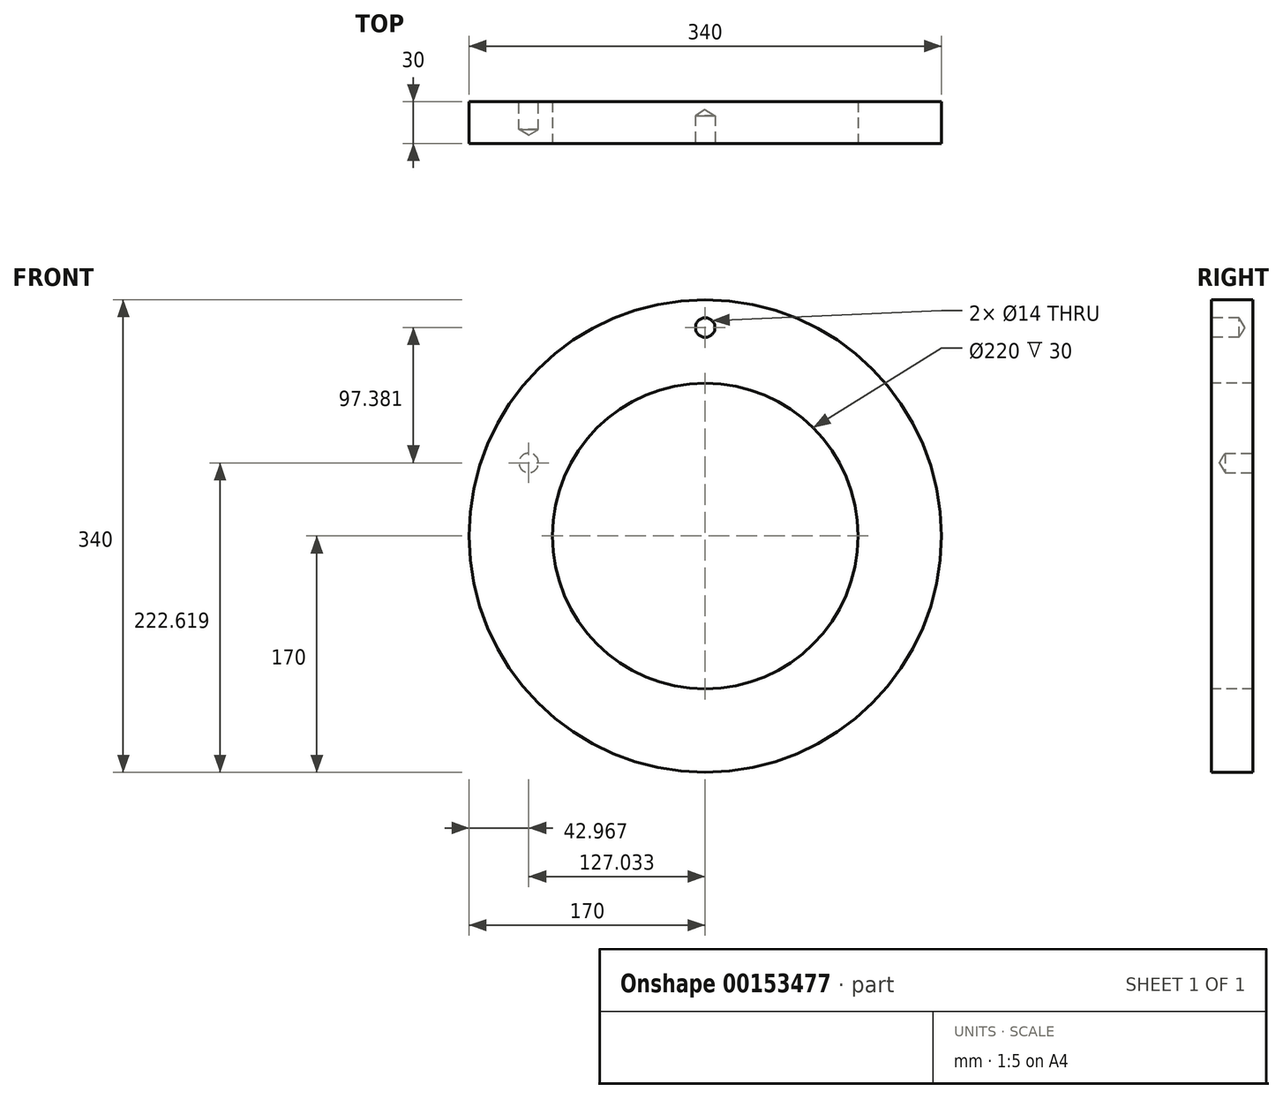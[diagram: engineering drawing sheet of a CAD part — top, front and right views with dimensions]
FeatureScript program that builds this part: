
annotation { "Feature Type Name" : "Feature", "Feature Type Description" : "" }
export const myFeature = defineFeature(function(context is Context, id is Id, definition is map)
    precondition{}
    {
        {
            var Q0;
            Q0=qCreatedBy(makeId("Front.planeOp"),FACE);
            var sketch = newSketch(context, id + "F0", { "sketchPlane" : qUnion([Q0])});
            skCircle(sketch, "E0", {"center": v(0, 0) * mm, "radius": 170 * mm});
            skCircle(sketch, "E1", {"center": v(0, 0) * mm, "radius": 150 * mm, "construction": true});
            skCircle(sketch, "E2", {"center": v(0, 0) * mm, "radius": 110 * mm});
            skLineSegment(sketch, "E3", {"start": v(0, 0) * mm, "end": v(-184.52, 0) * mm});
            skLineSegment(sketch, "E4", {"start": v(-184.52, 0) * mm, "end": v(252.94, 0) * mm, "construction": true});
            skLineSegment(sketch, "E5", {"start": v(0, 0) * mm, "end": v(0, 194.5) * mm});
            skLineSegment(sketch, "E6", {"start": v(0, 194.5) * mm, "end": v(0, -222.18) * mm, "construction": true});
            skCircle(sketch, "E7", {"center": v(0, 0) * mm, "radius": 137.5 * mm, "construction": true});
            skPoint(sketch, "E8", {"position": v(0, 137.5) * mm});
            skSolve(sketch);
        }
        {
            var Q0;
            Q0=makeQuery(id+"F0.imprint","IMPRINT",FACE,{"disambiguationData":[TD([[makeQuery(id+"F0.imprint","IMPRINT",EDGE,{"derivedFrom":sQuery(id+"F0.wireOp",EDGE,"E0")}),1.0]])]});
            extrude(context, id + "F1", {"entities" : qUnion([Q0]), "oppositeDirection" : true, "depth" : 30 * mm});
        }
        {
            var Q0;
            {var subQ0=sQuery(id+"F0.wireOp",EDGE,"E3");var subQ1=sQuery(id+"F0.wireOp",EDGE,"E0");var subQ2=makeQuery(id+"F0.imprint","INTERSECT",VERTEX,{"derivedFrom":[subQ1,subQ0]});Q0=makeQuery(id+"F0.imprint","IMPRINT",FACE,{"disambiguationData":[TD([[makeQuery(id+"F0.imprint","IMPRINT",EDGE,{"disambiguationData":[TD([[subQ2,-1.0]])],"derivedFrom":subQ1}),1.0]])]});}
            var sketch = newSketch(context, id + "F2", { "sketchPlane" : qUnion([Q0])});
            skPoint(sketch, "E9", {"position": v(0, 150) * mm});
            skSolve(sketch);
        }
        {
            var Q0;
            Q0=sQuery(id+"F2.wireOp",VERTEX,"E9");
            var Q1;
            Q1=makeQuery(id+"F1.opExtrude","SWEPT_BODY",BODY,{"disambiguationData":[OSD([sQuery(id+"F0.wireOp",EDGE,"E0"),sQuery(id+"F0.wireOp",EDGE,"E1")])]});
            hole(context, id + "F3", {"style" : HoleStyle.SIMPLE, "endStyle" : HoleEndStyle.BLIND, "standardTappedOrClearance" : lookupTablePath({ "standard" : "ISO", "engagement" : "75%", "pitch" : "2 mm", "size" : "M16", "type" : "Tapped" }), "standardBlindInLast" : lookupTablePath({ "standard" : "ISO", "engagement" : "75%", "pitch" : "2 mm", "size" : "M16", "type" : "Tapped" }), "holeDiameter" : 14 * mm, "holeDepth" : 20 * mm, "startFromSketch" : true, "locations" : qUnion([Q0]), "scope" : qUnion([Q1]), "majorDiameter" : 16 * mm});
        }
        {
            var Q0;
            Q0=makeQuery(id+"F1.opExtrude","CAP_FACE",FACE,{"disambiguationData":[OSD([sQuery(id+"F0.wireOp",EDGE,"E0"),sQuery(id+"F0.wireOp",EDGE,"E2")])],"isStart":false});
            var sketch = newSketch(context, id + "F4", { "sketchPlane" : qUnion([Q0])});
            skPoint(sketch, "E10", {"position": v(0, 138.02) * mm});
            skPoint(sketch, "E11", {"position": v(127.03, 52.62) * mm});
            skLineSegment(sketch, "E12", {"start": v(0, 0) * mm, "end": v(127.03, 52.62) * mm});
            skSolve(sketch);
        }
        {
            var Q0;
            Q0=sQuery(id+"F4.wireOp",VERTEX,"E11");
            var Q1;
            Q1=makeQuery(id+"F1.opExtrude","SWEPT_BODY",BODY,{"disambiguationData":[OSD([sQuery(id+"F0.wireOp",EDGE,"E0"),sQuery(id+"F0.wireOp",EDGE,"E2")])]});
            hole(context, id + "F5", {"style" : HoleStyle.SIMPLE, "endStyle" : HoleEndStyle.BLIND, "standardTappedOrClearance" : lookupTablePath({ "standard" : "ISO", "engagement" : "75%", "pitch" : "2 mm", "size" : "M16", "type" : "Tapped" }), "standardBlindInLast" : lookupTablePath({ "standard" : "ISO", "engagement" : "75%", "pitch" : "2 mm", "size" : "M16", "type" : "Tapped" }), "holeDiameter" : 14 * mm, "holeDepth" : 20 * mm, "locations" : qUnion([Q0]), "scope" : qUnion([Q1]), "majorDiameter" : 16 * mm});
        }
    });
